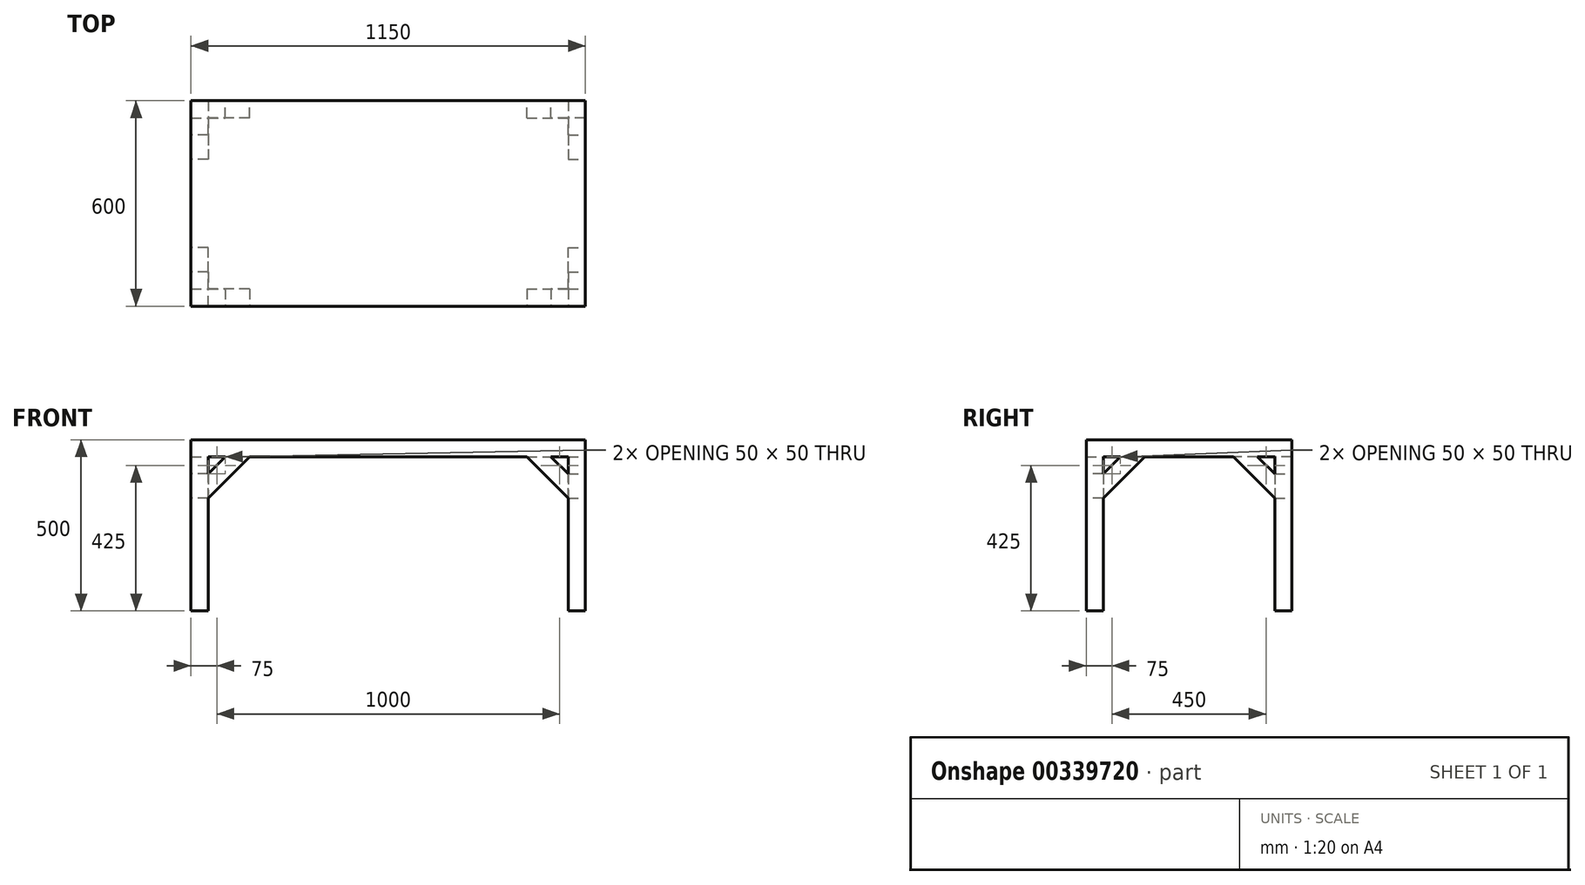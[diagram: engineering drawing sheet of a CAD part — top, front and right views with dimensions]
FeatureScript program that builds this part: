
annotation { "Feature Type Name" : "Feature", "Feature Type Description" : "" }
export const myFeature = defineFeature(function(context is Context, id is Id, definition is map)
    precondition{}
    {
        {
            var Q0;
            Q0=qCreatedBy(makeId("Top.planeOp"),FACE);
            var sketch = newSketch(context, id + "F0", { "sketchPlane" : qUnion([Q0])});
            skLineSegment(sketch, "E0.bottom", {"start": v(0, 0) * mm, "end": v(575, 0) * mm});
            skLineSegment(sketch, "E0.top", {"start": v(0, -300) * mm, "end": v(575, -300) * mm});
            skLineSegment(sketch, "E0.left", {"start": v(0, 0) * mm, "end": v(0, -300) * mm});
            skLineSegment(sketch, "E0.right", {"start": v(575, 0) * mm, "end": v(575, -300) * mm});
            skSolve(sketch);
        }
        {
            var Q0;
            Q0=makeQuery(id+"F0.imprint","IMPRINT",FACE,{"disambiguationData":[TD([[makeQuery(id+"F0.imprint","IMPRINT",EDGE,{"derivedFrom":sQuery(id+"F0.wireOp",EDGE,"E0.bottom")}),-1.0]])]});
            extrude(context, id + "F1", {"entities" : qUnion([Q0]), "oppositeDirection" : true, "depth" : 50 * mm});
        }
        {
            var Q0;
            Q0=makeQuery(id+"F1.opExtrude","CAP_FACE",FACE,{"disambiguationData":[OSD([sQuery(id+"F0.wireOp",EDGE,"E0.bottom"),sQuery(id+"F0.wireOp",EDGE,"E0.top"),sQuery(id+"F0.wireOp",EDGE,"E0.left"),sQuery(id+"F0.wireOp",EDGE,"E0.right")])],"isStart":false});
            var sketch = newSketch(context, id + "F2", { "sketchPlane" : qUnion([Q0])});
            skLineSegment(sketch, "E1.bottom", {"start": v(575, 300) * mm, "end": v(525, 300) * mm});
            skLineSegment(sketch, "E1.top", {"start": v(575, 250) * mm, "end": v(525, 250) * mm});
            skLineSegment(sketch, "E1.left", {"start": v(575, 300) * mm, "end": v(575, 250) * mm});
            skLineSegment(sketch, "E1.right", {"start": v(525, 300) * mm, "end": v(525, 250) * mm});
            skSolve(sketch);
        }
        {
            var Q0;
            Q0 = qSketchRegion(id + "F2", true);
            extrude(context, id + "F3", {"entities" : qUnion([Q0]), "operationType" : NewBodyOperationType.ADD, "depth" : 450 * mm});
        }
        {
            var Q0;
            Q0=makeQuery(id+"F3.boolean.opBoolean","MERGE",FACE,{"derivedFrom":[makeQuery(id+"F1.opExtrude","SWEPT_FACE",FACE,{"disambiguationData":[OSD([sQuery(id+"F0.wireOp",EDGE,"E0.top")])]}),makeQuery(id+"F3.opExtrude","SWEPT_FACE",FACE,{"disambiguationData":[OSD([sQuery(id+"F2.wireOp",EDGE,"E1.bottom")])]})]});
            var sketch = newSketch(context, id + "F4", { "sketchPlane" : qUnion([Q0])});
            skLineSegment(sketch, "E2", {"start": v(525, -100) * mm, "end": v(475, -50) * mm});
            skLineSegment(sketch, "E3", {"start": v(475, -50) * mm, "end": v(404.29, -50) * mm});
            skLineSegment(sketch, "E4", {"start": v(404.29, -50) * mm, "end": v(525, -170.71) * mm});
            skLineSegment(sketch, "E5", {"start": v(525, -170.71) * mm, "end": v(525, -100) * mm});
            skSolve(sketch);
        }
        {
            var Q0;
            Q0=makeQuery(id+"F4.imprint","IMPRINT",FACE,{"disambiguationData":[TD([[makeQuery(id+"F4.imprint","IMPRINT",EDGE,{"derivedFrom":sQuery(id+"F4.wireOp",EDGE,"E2")}),1.0]])]});
            var Q1;
            Q1=makeQuery(id+"F3.opExtrude","SWEPT_FACE",FACE,{"disambiguationData":[OSD([sQuery(id+"F2.wireOp",EDGE,"E1.top")])]});
            extrude(context, id + "F5", {"entities" : qUnion([Q0]), "operationType" : NewBodyOperationType.ADD, "endBound" : BoundingType.UP_TO_SURFACE, "oppositeDirection" : true, "endBoundEntityFace" : qUnion([Q1]), "depth" : 63 * mm});
        }
        {
            var Q0;
            Q0=makeQuery(id+"F3.boolean.opBoolean","MERGE",FACE,{"derivedFrom":[makeQuery(id+"F1.opExtrude","SWEPT_FACE",FACE,{"disambiguationData":[OSD([sQuery(id+"F0.wireOp",EDGE,"E0.right")])]}),makeQuery(id+"F3.opExtrude","SWEPT_FACE",FACE,{"disambiguationData":[OSD([sQuery(id+"F2.wireOp",EDGE,"E1.left")])]})]});
            var sketch = newSketch(context, id + "F6", { "sketchPlane" : qUnion([Q0])});
            skLineSegment(sketch, "E6", {"start": v(-250, -100) * mm, "end": v(-200, -50) * mm});
            skLineSegment(sketch, "E7", {"start": v(-200, -50) * mm, "end": v(-129.29, -50) * mm});
            skLineSegment(sketch, "E8", {"start": v(-129.29, -50) * mm, "end": v(-250, -170.71) * mm});
            skLineSegment(sketch, "E9", {"start": v(-250, -170.71) * mm, "end": v(-250, -100) * mm});
            skSolve(sketch);
        }
        {
            var Q0;
            Q0=makeQuery(id+"F6.imprint","IMPRINT",FACE,{"disambiguationData":[TD([[makeQuery(id+"F6.imprint","IMPRINT",EDGE,{"derivedFrom":sQuery(id+"F6.wireOp",EDGE,"E6")}),-1.0]])]});
            var Q1;
            {var subQ1=sQuery(id+"F2.wireOp",EDGE,"E1.right");var subQ3=sQuery(id+"F4.wireOp",EDGE,"E4");Q1=makeQuery(id+"F5.boolean.opBoolean","SPLIT",FACE,{"disambiguationData":[TD([makeQuery(id+"F5.opExtrude","SWEPT_FACE",FACE,{"disambiguationData":[OSD([subQ3])]})])],"derivedFrom":makeQuery(id+"F3.opExtrude","SWEPT_FACE",FACE,{"disambiguationData":[OSD([subQ1])]})});}
            extrude(context, id + "F7", {"entities" : qUnion([Q0]), "operationType" : NewBodyOperationType.ADD, "endBound" : BoundingType.UP_TO_SURFACE, "oppositeDirection" : true, "endBoundEntityFace" : qUnion([Q1]), "depth" : 25 * mm});
        }
        {
            var Q0;
            Q0=makeQuery(id+"F1.opExtrude","SWEPT_BODY",BODY,{"disambiguationData":[OSD([sQuery(id+"F0.wireOp",EDGE,"E0.bottom"),sQuery(id+"F0.wireOp",EDGE,"E0.top"),sQuery(id+"F0.wireOp",EDGE,"E0.left"),sQuery(id+"F0.wireOp",EDGE,"E0.right")])]});
            var Q1;
            Q1=qCreatedBy(makeId("Right.planeOp"),FACE);
            mirror(context, id + "F8", {"operationType" : NewBodyOperationType.ADD, "entities" : qUnion([Q0]), "mirrorPlane" : qUnion([Q1])});
        }
        {
            var Q0;
            Q0=makeQuery(id+"F1.opExtrude","SWEPT_BODY",BODY,{"disambiguationData":[OSD([sQuery(id+"F0.wireOp",EDGE,"E0.bottom"),sQuery(id+"F0.wireOp",EDGE,"E0.top"),sQuery(id+"F0.wireOp",EDGE,"E0.left"),sQuery(id+"F0.wireOp",EDGE,"E0.right")])]});
            var Q1;
            Q1=qCreatedBy(makeId("Front.planeOp"),FACE);
            mirror(context, id + "F9", {"operationType" : NewBodyOperationType.ADD, "entities" : qUnion([Q0]), "mirrorPlane" : qUnion([Q1])});
        }
    });
